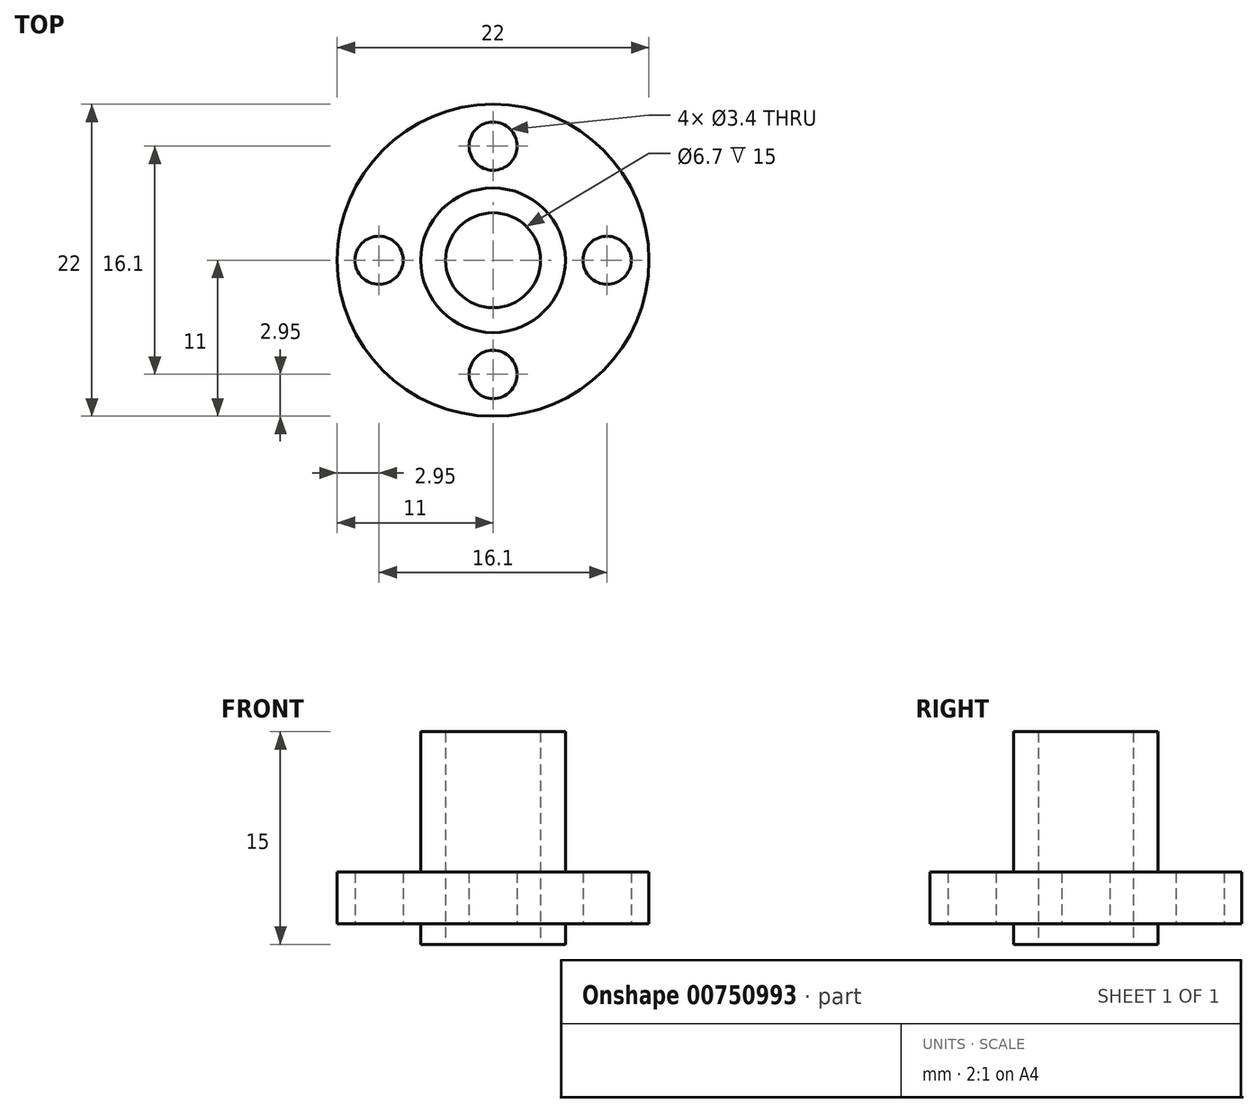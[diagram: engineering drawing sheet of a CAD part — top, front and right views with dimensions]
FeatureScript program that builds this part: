
annotation { "Feature Type Name" : "Feature", "Feature Type Description" : "" }
export const myFeature = defineFeature(function(context is Context, id is Id, definition is map)
    precondition{}
    {
        {
            var Q0;
            Q0=qCreatedBy(makeId("Top.planeOp"),FACE);
            var sketch = newSketch(context, id + "F0", { "sketchPlane" : qUnion([Q0])});
            skCircle(sketch, "E0", {"center": v(0, 0) * mm, "radius": 5.1 * mm});
            skCircle(sketch, "E1", {"center": v(0, 0) * mm, "radius": 11 * mm});
            skLineSegment(sketch, "E2", {"start": v(0, 0) * mm, "end": v(9.75, 0) * mm, "construction": true});
            skCircle(sketch, "E3", {"center": v(8.05, 0) * mm, "radius": 1.7 * mm});
            skPoint(sketch, "E3.second.point", {"position": v(6.35, 0) * mm});
            skPoint(sketch, "E3.third.point", {"position": v(8.16, -1.7) * mm});
            skLineSegment(sketch, "E4.1.0", {"start": v(0, 0) * mm, "end": v(0, 9.75) * mm, "construction": true});
            skCircle(sketch, "E4.1.1", {"center": v(0, 8.05) * mm, "radius": 1.7 * mm});
            skLineSegment(sketch, "E4.2.0", {"start": v(0, 0) * mm, "end": v(-9.75, 0) * mm, "construction": true});
            skCircle(sketch, "E4.2.1", {"center": v(-8.05, 0) * mm, "radius": 1.7 * mm});
            skLineSegment(sketch, "E4.3.0", {"start": v(0, 0) * mm, "end": v(0, -9.75) * mm, "construction": true});
            skCircle(sketch, "E4.3.1", {"center": v(0, -8.05) * mm, "radius": 1.7 * mm});
            skCircle(sketch, "E5.0", {"center": v(0, 0) * mm, "radius": 3.35 * mm});
            skSolve(sketch);
        }
        {
            var Q0;
            Q0=makeQuery(id+"F0.imprint","IMPRINT",FACE,{"disambiguationData":[TD([[makeQuery(id+"F0.imprint","IMPRINT",EDGE,{"derivedFrom":sQuery(id+"F0.wireOp",EDGE,"E0")}),1.0]])]});
            var Q1;
            Q1=sQuery(id+"F0.wireOp",EDGE,"E4.3.0");
            var Q2;
            Q2=sQuery(id+"F0.wireOp",EDGE,"E4.1.0");
            var Q3;
            Q3=sQuery(id+"F0.wireOp",EDGE,"E4.2.0");
            var Q4;
            Q4=sQuery(id+"F0.wireOp",EDGE,"E2");
            extrude(context, id + "F1", {"entities" : qUnion([Q0]), "surfaceEntities" : qUnion([Q1, Q2, Q3, Q4]), "depth" : 15 * mm, "offsetDistance" : 25 * mm});
        }
        {
            var Q0;
            Q0=makeQuery(id+"F0.imprint","IMPRINT",FACE,{"disambiguationData":[TD([[makeQuery(id+"F0.imprint","IMPRINT",EDGE,{"derivedFrom":sQuery(id+"F0.wireOp",EDGE,"E0")}),-1.0]])]});
            extrude(context, id + "F2", {"entities" : qUnion([Q0]), "operationType" : NewBodyOperationType.ADD, "depth" : 5.1 * mm, "offsetDistance" : 25 * mm, "hasSecondDirection" : true, "secondDirectionOppositeDirection" : false, "secondDirectionDepth" : 1.45 * mm});
        }
    });
